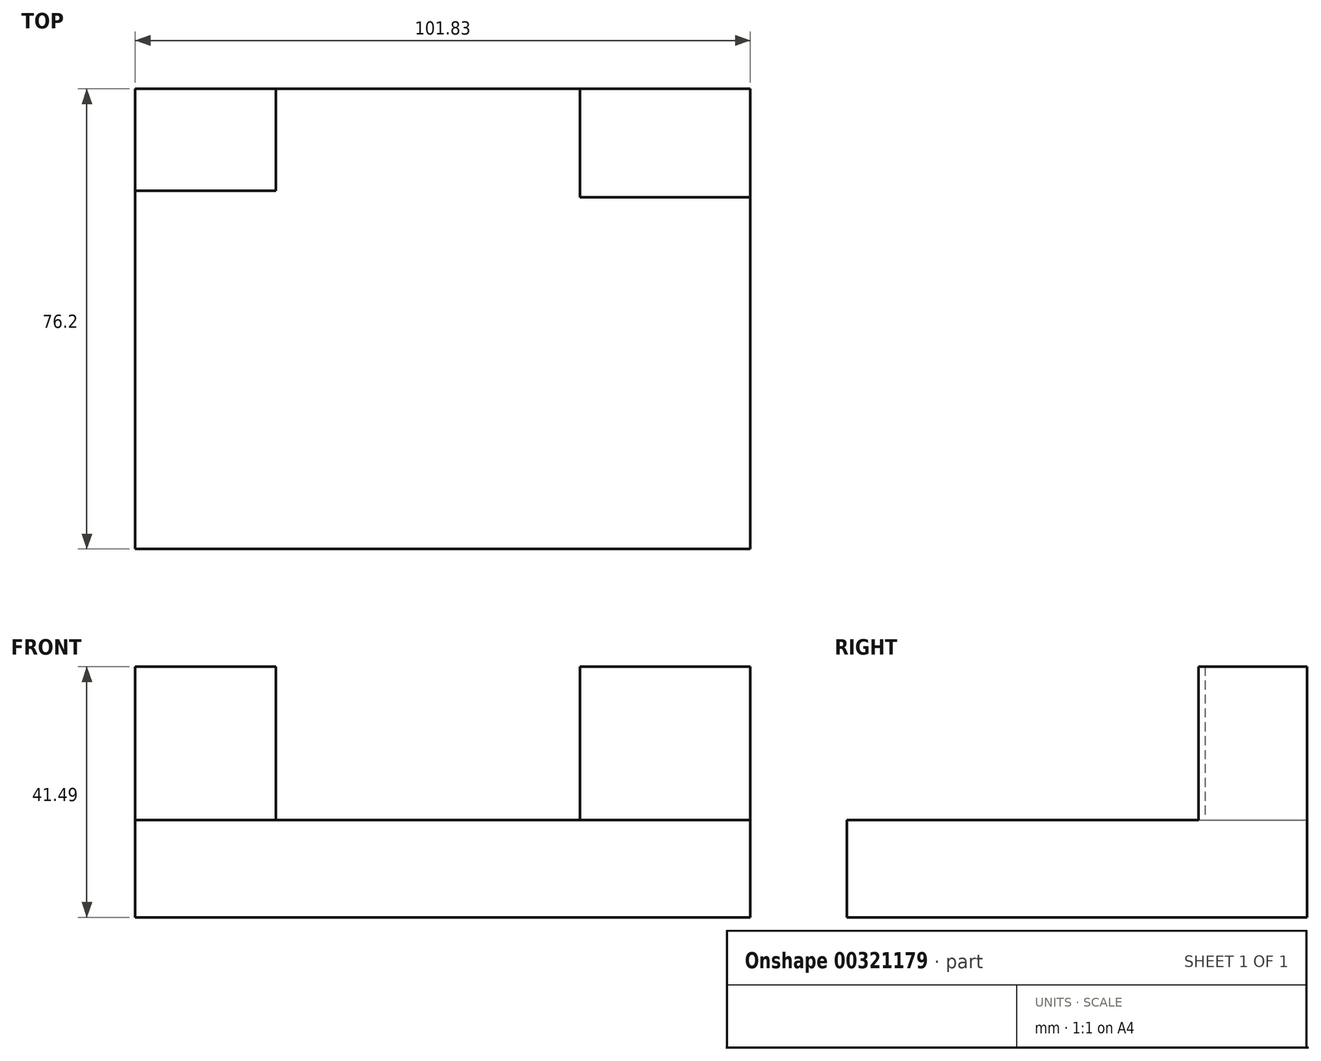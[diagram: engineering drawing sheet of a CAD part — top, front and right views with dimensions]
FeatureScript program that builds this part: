
annotation { "Feature Type Name" : "Feature", "Feature Type Description" : "" }
export const myFeature = defineFeature(function(context is Context, id is Id, definition is map)
    precondition{}
    {
        {
            var Q0;
            Q0=qCreatedBy(makeId("Front.planeOp"),FACE);
            var sketch = newSketch(context, id + "F0", { "sketchPlane" : qUnion([Q0])});
            skLineSegment(sketch, "E0", {"start": v(-39.93, -40.7) * mm, "end": v(61.9, -40.7) * mm});
            skLineSegment(sketch, "E1", {"start": v(61.9, -40.7) * mm, "end": v(61.9, -24.6) * mm});
            skLineSegment(sketch, "E2", {"start": v(61.9, -24.6) * mm, "end": v(-39.93, -24.6) * mm});
            skLineSegment(sketch, "E3", {"start": v(-39.93, -24.6) * mm, "end": v(-39.93, -40.7) * mm});
            skSolve(sketch);
        }
        {
            var Q0;
            Q0=makeQuery(id+"F0.imprint","IMPRINT",FACE,{"disambiguationData":[TD([[makeQuery(id+"F0.imprint","IMPRINT",EDGE,{"derivedFrom":sQuery(id+"F0.wireOp",EDGE,"E0")}),1.0]])]});
            extrude(context, id + "F1", {"entities" : qUnion([Q0]), "depth" : 76.2 * mm});
        }
        {
            var Q0;
            Q0=makeQuery(id+"F1.opExtrude","SWEPT_FACE",FACE,{"disambiguationData":[OSD([sQuery(id+"F0.wireOp",EDGE,"E2")])]});
            var sketch = newSketch(context, id + "F2", { "sketchPlane" : qUnion([Q0])});
            skLineSegment(sketch, "E4.bottom", {"start": v(61.9, -17.98) * mm, "end": v(33.7, -17.98) * mm});
            skLineSegment(sketch, "E4.top", {"start": v(61.9, 0) * mm, "end": v(33.7, 0) * mm});
            skLineSegment(sketch, "E4.left", {"start": v(61.9, -17.98) * mm, "end": v(61.9, 0) * mm});
            skLineSegment(sketch, "E4.right", {"start": v(33.7, -17.98) * mm, "end": v(33.7, 0) * mm});
            skSolve(sketch);
        }
        {
            var Q0;
            Q0 = qSketchRegion(id + "F2", true);
            extrude(context, id + "F3", {"entities" : qUnion([Q0]), "operationType" : NewBodyOperationType.ADD, "depth" : 25.4 * mm});
        }
        {
            var Q0;
            Q0=makeQuery(id+"F1.opExtrude","SWEPT_FACE",FACE,{"disambiguationData":[OSD([sQuery(id+"F0.wireOp",EDGE,"E2")])]});
            var sketch = newSketch(context, id + "F4", { "sketchPlane" : qUnion([Q0])});
            skLineSegment(sketch, "E5.bottom", {"start": v(-39.93, -16.88) * mm, "end": v(-16.65, -16.88) * mm});
            skLineSegment(sketch, "E5.top", {"start": v(-39.93, 0) * mm, "end": v(-16.65, 0) * mm});
            skLineSegment(sketch, "E5.left", {"start": v(-39.93, -16.88) * mm, "end": v(-39.93, 0) * mm});
            skLineSegment(sketch, "E5.right", {"start": v(-16.65, -16.88) * mm, "end": v(-16.65, 0) * mm});
            skSolve(sketch);
        }
        {
            var Q0;
            Q0 = qSketchRegion(id + "F4", true);
            extrude(context, id + "F5", {"entities" : qUnion([Q0]), "operationType" : NewBodyOperationType.ADD, "depth" : 25.4 * mm});
        }
    });
